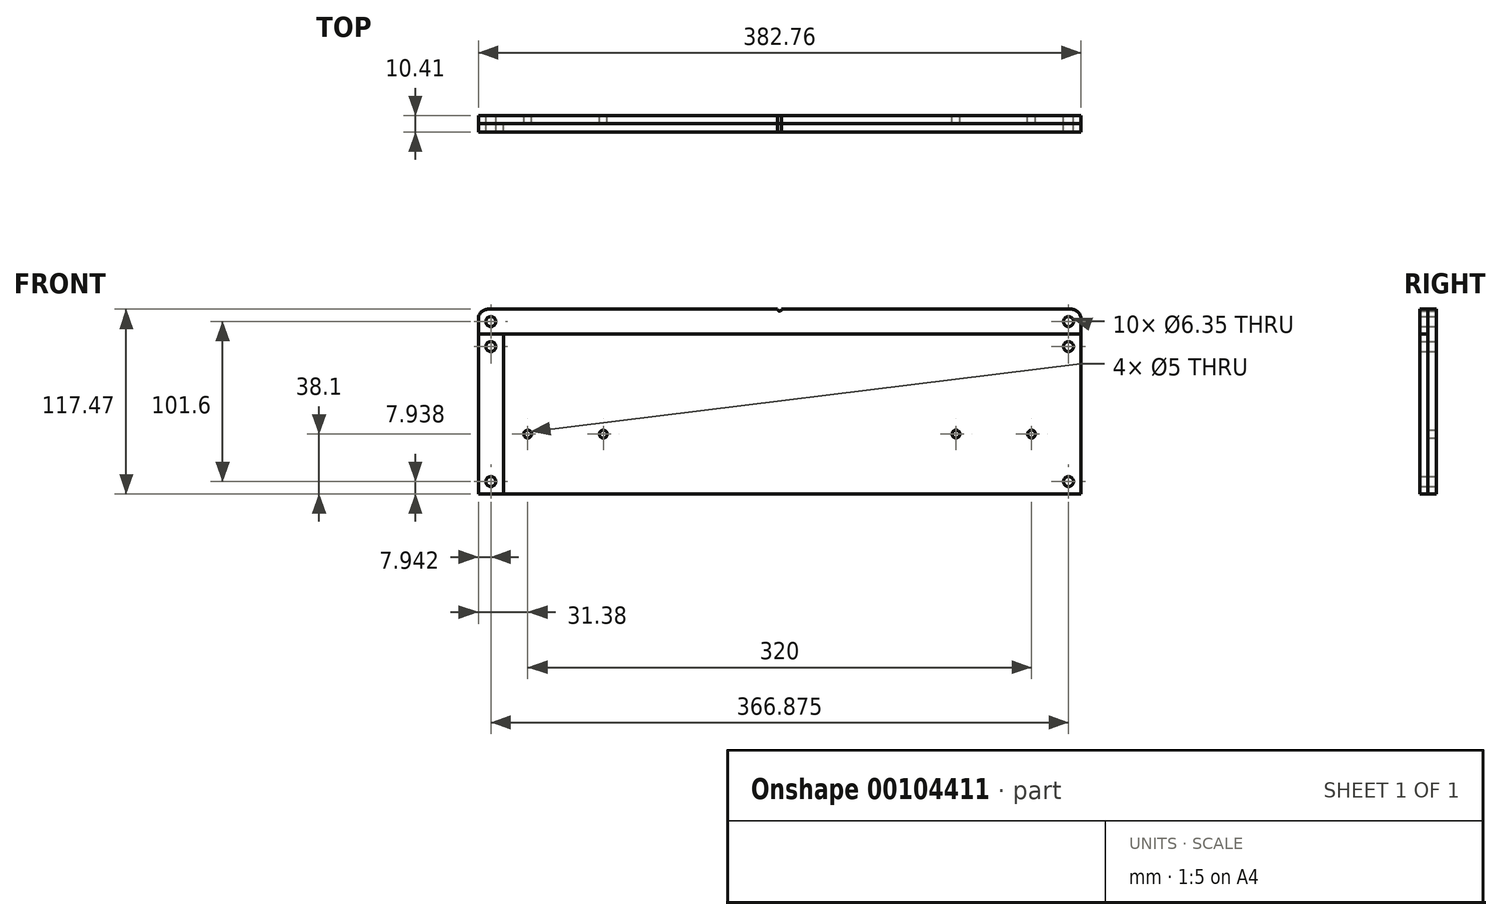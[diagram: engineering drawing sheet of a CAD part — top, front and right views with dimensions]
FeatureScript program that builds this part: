
annotation { "Feature Type Name" : "Feature", "Feature Type Description" : "" }
export const myFeature = defineFeature(function(context is Context, id is Id, definition is map)
    precondition{}
    {
        {
            assignVariable(context, id + "F0", {"variableType" : VariableType.LENGTH, "name" : "ply", "lengthValue" : 5.2 * mm});
        }
        {
            var Q0;
            Q0=qCreatedBy(makeId("Front.planeOp"),FACE);
            var sketch = newSketch(context, id + "F1", { "sketchPlane" : qUnion([Q0])});
            skLineSegment(sketch, "E0.bottom", {"start": v(-191.38, 0) * mm, "end": v(191.38, 0) * mm});
            skLineSegment(sketch, "E0.top", {"start": v(-191.38, 117.48) * mm, "end": v(191.38, 117.48) * mm});
            skLineSegment(sketch, "E0.left", {"start": v(-191.38, 0) * mm, "end": v(-191.38, 117.47) * mm});
            skLineSegment(sketch, "E0.right", {"start": v(191.38, 0) * mm, "end": v(191.38, 117.47) * mm});
            skLineSegment(sketch, "E1", {"start": v(-191.38, 101.6) * mm, "end": v(191.38, 101.6) * mm, "construction": true});
            skCircle(sketch, "E2", {"center": v(-112, 38.1) * mm, "radius": 2.5 * mm});
            skLineSegment(sketch, "E3", {"start": v(0, 0) * mm, "end": v(0, 117.48) * mm, "construction": true});
            skLineSegment(sketch, "E4", {"start": v(-112, 38.1) * mm, "end": v(0, 38.1) * mm, "construction": true});
            skLineSegment(sketch, "E5", {"start": v(0, 38.1) * mm, "end": v(112, 38.1) * mm, "construction": true});
            skCircle(sketch, "E6", {"center": v(112, 38.1) * mm, "radius": 2.5 * mm});
            skCircle(sketch, "E7", {"center": v(160, 38.1) * mm, "radius": 2.5 * mm});
            skCircle(sketch, "E8", {"center": v(-160, 38.1) * mm, "radius": 2.5 * mm});
            skLineSegment(sketch, "E9", {"start": v(-160, 38.1) * mm, "end": v(-112, 38.1) * mm, "construction": true});
            skLineSegment(sketch, "E10", {"start": v(112, 38.1) * mm, "end": v(160, 38.1) * mm, "construction": true});
            skLineSegment(sketch, "E11", {"start": v(-175.5, 101.6) * mm, "end": v(-175.5, 0) * mm, "construction": true});
            skLineSegment(sketch, "E12", {"start": v(175.5, 101.6) * mm, "end": v(175.5, 0) * mm, "construction": true});
            skLineSegment(sketch, "E13", {"start": v(-191.38, 117.47) * mm, "end": v(-175.5, 101.6) * mm, "construction": true});
            skCircle(sketch, "E14", {"center": v(-183.44, 109.54) * mm, "radius": 3.18 * mm});
            skLineSegment(sketch, "E15", {"start": v(-175.5, 101.6) * mm, "end": v(-191.38, 85.72) * mm, "construction": true});
            skLineSegment(sketch, "E16", {"start": v(-175.5, 0) * mm, "end": v(-191.38, 15.88) * mm, "construction": true});
            skCircle(sketch, "E17", {"center": v(-183.44, 93.66) * mm, "radius": 3.18 * mm});
            skCircle(sketch, "E18", {"center": v(-183.44, 7.94) * mm, "radius": 3.18 * mm});
            skCircle(sketch, "E19.MirrorC", {"center": v(183.44, 7.94) * mm, "radius": 3.18 * mm});
            skCircle(sketch, "E20.MirrorC", {"center": v(183.44, 93.66) * mm, "radius": 3.18 * mm});
            skCircle(sketch, "E21.MirrorC", {"center": v(183.44, 109.54) * mm, "radius": 3.18 * mm});
            skSolve(sketch);
        }
        {
            var Q0;
            Q0=qCreatedBy(makeId("Front.planeOp"),FACE);
            var sketch = newSketch(context, id + "F2", { "sketchPlane" : qUnion([Q0])});
            skLineSegment(sketch, "E22.0", {"start": v(-185.03, 117.48) * mm, "end": v(-1.27, 117.48) * mm});
            skLineSegment(sketch, "E22.1", {"start": v(-191.38, 0) * mm, "end": v(-191.38, 111.13) * mm});
            skLineSegment(sketch, "E22.2", {"start": v(-191.38, 0) * mm, "end": v(191.38, 0) * mm});
            skLineSegment(sketch, "E22.3", {"start": v(191.38, 0) * mm, "end": v(191.38, 111.13) * mm});
            skCircle(sketch, "E22.4", {"center": v(160, 38.1) * mm, "radius": 2.5 * mm});
            skCircle(sketch, "E22.5", {"center": v(112, 38.1) * mm, "radius": 2.5 * mm});
            skCircle(sketch, "E22.6", {"center": v(-112, 38.1) * mm, "radius": 2.5 * mm});
            skCircle(sketch, "E22.7", {"center": v(-160, 38.1) * mm, "radius": 2.5 * mm});
            skArc(sketch, "E23", {"start": v(-1.27, 117.48) * mm, "mid": v(0, 116.2) * mm, "end": v(1.27, 117.48) * mm});
            skLineSegment(sketch, "E24.trimOffspring", {"start": v(1.27, 117.48) * mm, "end": v(185.02, 117.48) * mm});
            skCircle(sketch, "E25.0", {"center": v(-183.44, 109.54) * mm, "radius": 3.18 * mm});
            skCircle(sketch, "E25.1", {"center": v(183.44, 109.54) * mm, "radius": 3.18 * mm});
            skPoint(sketch, "E26.visualSharp", {"position": v(-191.38, 117.48) * mm});
            skArc(sketch, "E26.filletArc", {"start": v(-185.03, 117.47) * mm, "mid": v(-189.52, 115.62) * mm, "end": v(-191.38, 111.13) * mm});
            skPoint(sketch, "E27.visualSharp", {"position": v(191.38, 117.48) * mm});
            skArc(sketch, "E27.filletArc", {"start": v(191.37, 111.13) * mm, "mid": v(189.52, 115.62) * mm, "end": v(185.02, 117.48) * mm});
            skCircle(sketch, "E28.0", {"center": v(-183.44, 93.66) * mm, "radius": 3.18 * mm});
            skCircle(sketch, "E28.1", {"center": v(-183.44, 7.94) * mm, "radius": 3.18 * mm});
            skCircle(sketch, "E28.2", {"center": v(183.44, 7.94) * mm, "radius": 3.18 * mm});
            skCircle(sketch, "E28.3", {"center": v(183.44, 93.66) * mm, "radius": 3.18 * mm});
            skSolve(sketch);
        }
        {
            var Q0;
            Q0 = qSketchRegion(id + "F2", true);
            extrude(context, id + "F3", {"entities" : qUnion([Q0]), "depth" : getVariable(context, 'ply'), "offsetDistance" : 25.4 * mm});
        }
        {
            var Q0;
            Q0=makeQuery(id+"F3.opExtrude","CAP_FACE",FACE,{"disambiguationData":[OSD([sQuery(id+"F2.wireOp",EDGE,"E22.0"),sQuery(id+"F2.wireOp",EDGE,"E22.1"),sQuery(id+"F2.wireOp",EDGE,"E22.2"),sQuery(id+"F2.wireOp",EDGE,"E22.3"),sQuery(id+"F2.wireOp",EDGE,"E22.4"),sQuery(id+"F2.wireOp",EDGE,"E22.5"),sQuery(id+"F2.wireOp",EDGE,"E22.6"),sQuery(id+"F2.wireOp",EDGE,"E22.7"),sQuery(id+"F2.wireOp",EDGE,"E23"),sQuery(id+"F2.wireOp",EDGE,"E24.trimOffspring"),sQuery(id+"F2.wireOp",EDGE,"E25.0"),sQuery(id+"F2.wireOp",EDGE,"E25.1"),sQuery(id+"F2.wireOp",EDGE,"E26.filletArc"),sQuery(id+"F2.wireOp",EDGE,"E27.filletArc"),sQuery(id+"F2.wireOp",EDGE,"7aa5f786-9224-470f-a4e9-794633869a8b.filletArc"),sQuery(id+"F2.wireOp",EDGE,"c04e4ba6-30d1-4b17-a345-159325f8e2e9.filletArc")])],"isStart":false});
            var sketch = newSketch(context, id + "F4", { "sketchPlane" : qUnion([Q0])});
            skArc(sketch, "E29.0.0", {"start": v(1.27, 117.48) * mm, "mid": v(0, 116.2) * mm, "end": v(-1.27, 117.48) * mm});
            skLineSegment(sketch, "E29.0.1", {"start": v(-1.27, 117.48) * mm, "end": v(-185.03, 117.48) * mm});
            skArc(sketch, "E29.0.2", {"start": v(-185.03, 117.47) * mm, "mid": v(-189.52, 115.62) * mm, "end": v(-191.38, 111.13) * mm});
            skLineSegment(sketch, "E29.0.3", {"start": v(-191.38, 111.13) * mm, "end": v(-191.38, 101.6) * mm});
            skLineSegment(sketch, "E29.0.7", {"start": v(191.38, 101.6) * mm, "end": v(191.38, 111.13) * mm});
            skArc(sketch, "E29.0.8", {"start": v(191.37, 111.13) * mm, "mid": v(189.52, 115.62) * mm, "end": v(185.02, 117.48) * mm});
            skLineSegment(sketch, "E29.0.9", {"start": v(185.02, 117.48) * mm, "end": v(1.27, 117.48) * mm});
            skLineSegment(sketch, "E30.0", {"start": v(-191.38, 101.6) * mm, "end": v(191.38, 101.6) * mm});
            skPoint(sketch, "E29.0.6.start.orphan", {"position": v(-191.38, 0) * mm});
            skCircle(sketch, "E31.0", {"center": v(-183.44, 109.54) * mm, "radius": 3.18 * mm});
            skCircle(sketch, "E31.1", {"center": v(183.44, 109.54) * mm, "radius": 3.18 * mm});
            skSolve(sketch);
        }
        {
            var Q0;
            Q0 = qSketchRegion(id + "F4", true);
            extrude(context, id + "F5", {"entities" : qUnion([Q0]), "depth" : getVariable(context, 'ply'), "offsetDistance" : 25.4 * mm});
        }
        {
            var Q0;
            Q0=makeQuery(id+"F3.opExtrude","CAP_FACE",FACE,{"disambiguationData":[OSD([sQuery(id+"F2.wireOp",EDGE,"E22.0"),sQuery(id+"F2.wireOp",EDGE,"E22.1"),sQuery(id+"F2.wireOp",EDGE,"E22.2"),sQuery(id+"F2.wireOp",EDGE,"E22.3"),sQuery(id+"F2.wireOp",EDGE,"E22.4"),sQuery(id+"F2.wireOp",EDGE,"E22.5"),sQuery(id+"F2.wireOp",EDGE,"E22.6"),sQuery(id+"F2.wireOp",EDGE,"E22.7"),sQuery(id+"F2.wireOp",EDGE,"E23"),sQuery(id+"F2.wireOp",EDGE,"E24.trimOffspring"),sQuery(id+"F2.wireOp",EDGE,"E25.0"),sQuery(id+"F2.wireOp",EDGE,"E25.1"),sQuery(id+"F2.wireOp",EDGE,"E26.filletArc"),sQuery(id+"F2.wireOp",EDGE,"E27.filletArc")])],"isStart":false});
            var sketch = newSketch(context, id + "F6", { "sketchPlane" : qUnion([Q0])});
            skLineSegment(sketch, "E32.0", {"start": v(-175.5, 101.6) * mm, "end": v(-175.5, 0) * mm});
            skCircle(sketch, "E32.1", {"center": v(-183.44, 7.94) * mm, "radius": 3.18 * mm});
            skCircle(sketch, "E32.2", {"center": v(-183.44, 93.66) * mm, "radius": 3.18 * mm});
            skLineSegment(sketch, "E32.3", {"start": v(-191.38, 0) * mm, "end": v(-191.38, 101.6) * mm});
            skLineSegment(sketch, "E33", {"start": v(-175.5, 101.6) * mm, "end": v(-191.38, 101.6) * mm});
            skLineSegment(sketch, "E34", {"start": v(-175.5, 0) * mm, "end": v(-191.38, 0) * mm});
            skSolve(sketch);
        }
        {
            var Q0;
            Q0 = qSketchRegion(id + "F6", true);
            extrude(context, id + "F7", {"entities" : qUnion([Q0]), "depth" : getVariable(context, 'ply'), "offsetDistance" : 25.4 * mm});
        }
    });
